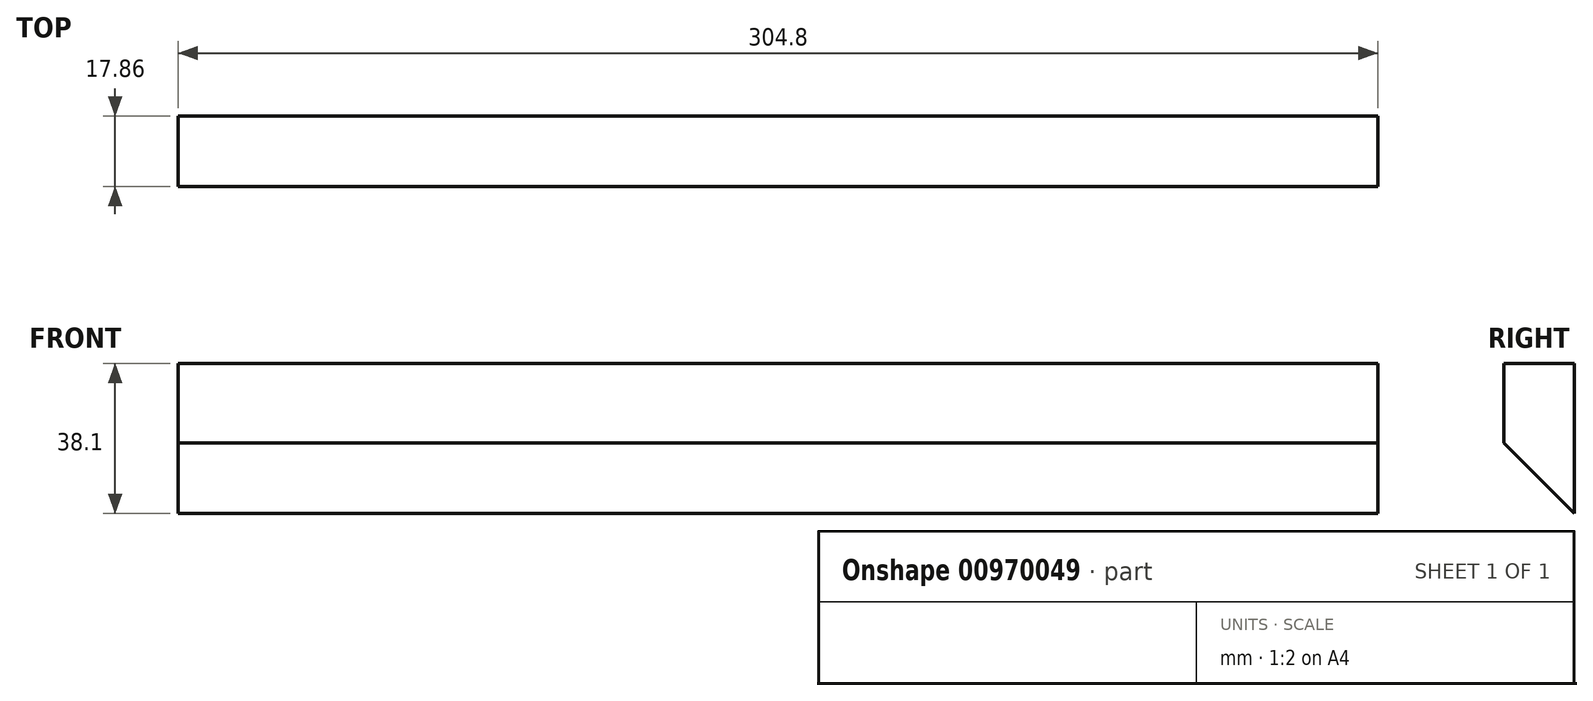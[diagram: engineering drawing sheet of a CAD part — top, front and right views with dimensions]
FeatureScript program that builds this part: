
annotation { "Feature Type Name" : "Feature", "Feature Type Description" : "" }
export const myFeature = defineFeature(function(context is Context, id is Id, definition is map)
    precondition{}
    {
        {
            var Q0;
            Q0=qCreatedBy(makeId("Right.planeOp"),FACE);
            var sketch = newSketch(context, id + "F0", { "sketchPlane" : qUnion([Q0])});
            skPoint(sketch, "E0.middle", {"position": v(0, 0) * mm});
            skLineSegment(sketch, "E1", {"start": v(0, 0) * mm, "end": v(0, 38.1) * mm});
            skLineSegment(sketch, "E2", {"start": v(0, 38.1) * mm, "end": v(-17.86, 38.1) * mm});
            skLineSegment(sketch, "E3", {"start": v(-17.86, 38.1) * mm, "end": v(-17.86, 17.86) * mm});
            skLineSegment(sketch, "E4", {"start": v(-17.86, 17.86) * mm, "end": v(0, 0) * mm});
            skSolve(sketch);
        }
        {
            var Q0;
            Q0=qSketchRegion(id+"F0",true);
            extrude(context, id + "F1", {"entities" : qUnion([Q0]), "endBound" : BoundingType.SYMMETRIC, "depth" : 304.8 * mm, "offsetDistance" : 25.4 * mm});
        }
    });
